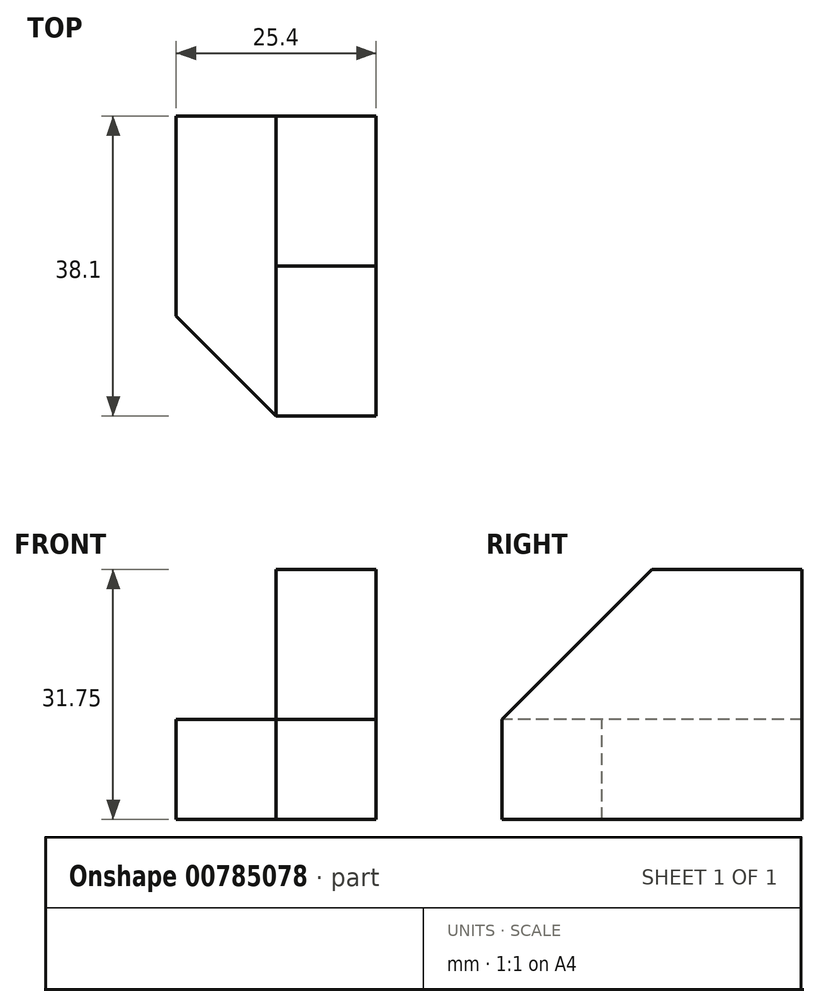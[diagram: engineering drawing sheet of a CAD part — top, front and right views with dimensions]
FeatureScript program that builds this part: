
annotation { "Feature Type Name" : "Feature", "Feature Type Description" : "" }
export const myFeature = defineFeature(function(context is Context, id is Id, definition is map)
    precondition{}
    {
        {
            var Q0;
            Q0=qCreatedBy(makeId("Front.planeOp"),FACE);
            var sketch = newSketch(context, id + "F0", { "sketchPlane" : qUnion([Q0])});
            skLineSegment(sketch, "E0", {"start": v(0, 0) * mm, "end": v(25.4, 0) * mm});
            skLineSegment(sketch, "E1", {"start": v(25.4, 0) * mm, "end": v(25.4, 31.75) * mm});
            skLineSegment(sketch, "E2", {"start": v(25.4, 31.75) * mm, "end": v(0, 31.75) * mm});
            skLineSegment(sketch, "E3", {"start": v(0, 31.75) * mm, "end": v(0, 0) * mm});
            skSolve(sketch);
        }
        {
            var Q0;
            Q0=makeQuery(id+"F0.imprint","IMPRINT",FACE,{"disambiguationData":[TD([[makeQuery(id+"F0.imprint","IMPRINT",EDGE,{"derivedFrom":sQuery(id+"F0.wireOp",EDGE,"E0")}),1.0]])]});
            extrude(context, id + "F1", {"entities" : qUnion([Q0]), "depth" : 38.1 * mm, "offsetDistance" : 25.4 * mm});
        }
        {
            var Q0;
            Q0=makeQuery(id+"F1.opExtrude","CAP_FACE",FACE,{"disambiguationData":[OSD([sQuery(id+"F0.wireOp",EDGE,"E0"),sQuery(id+"F0.wireOp",EDGE,"E1"),sQuery(id+"F0.wireOp",EDGE,"E2"),sQuery(id+"F0.wireOp",EDGE,"E3")])],"isStart":false});
            var sketch = newSketch(context, id + "F2", { "sketchPlane" : qUnion([Q0])});
            skLineSegment(sketch, "E4", {"start": v(25.4, 31.75) * mm, "end": v(12.7, 31.75) * mm});
            skLineSegment(sketch, "E5", {"start": v(12.7, 31.75) * mm, "end": v(12.7, 12.7) * mm});
            skLineSegment(sketch, "E6", {"start": v(12.7, 12.7) * mm, "end": v(0, 12.7) * mm});
            skSolve(sketch);
        }
        {
            var Q0;
            {var subQ0=sQuery(id+"F2.wireOp",EDGE,"E5");Q0=makeQuery(id+"F2.imprint","IMPRINT",FACE,{"disambiguationData":[TD([[makeQuery(id+"F2.imprint","IMPRINT",EDGE,{"derivedFrom":subQ0}),-1.0]])]});}
            extrude(context, id + "F3", {"entities" : qUnion([Q0]), "operationType" : NewBodyOperationType.REMOVE, "oppositeDirection" : true, "depth" : 38.1 * mm, "offsetDistance" : 25.4 * mm});
        }
        {
            var Q0;
            Q0=makeQuery(id+"F3.boolean.opBoolean","COPY",FACE,{"derivedFrom":makeQuery(id+"F3.opExtrude","SWEPT_FACE",FACE,{"disambiguationData":[OSD([sQuery(id+"F2.wireOp",EDGE,"E5")])]})});
            var sketch = newSketch(context, id + "F4", { "sketchPlane" : qUnion([Q0])});
            skLineSegment(sketch, "E7", {"start": v(38.1, 31.75) * mm, "end": v(19.05, 31.75) * mm});
            skLineSegment(sketch, "E8", {"start": v(19.05, 31.75) * mm, "end": v(38.1, 12.7) * mm});
            skSolve(sketch);
        }
        {
            var Q0;
            Q0=makeQuery(id+"F4.imprint","IMPRINT",FACE,{"disambiguationData":[TD([[makeQuery(id+"F4.imprint","IMPRINT",EDGE,{"derivedFrom":sQuery(id+"F4.wireOp",EDGE,"E7")}),-1.0]])]});
            extrude(context, id + "F5", {"entities" : qUnion([Q0]), "operationType" : NewBodyOperationType.REMOVE, "oppositeDirection" : true, "depth" : 25.4 * mm, "offsetDistance" : 25.4 * mm});
        }
        {
            var Q0;
            Q0=makeQuery(id+"F3.boolean.opBoolean","COPY",FACE,{"derivedFrom":makeQuery(id+"F3.opExtrude","SWEPT_FACE",FACE,{"disambiguationData":[OSD([sQuery(id+"F2.wireOp",EDGE,"E6")])]})});
            var sketch = newSketch(context, id + "F6", { "sketchPlane" : qUnion([Q0])});
            skLineSegment(sketch, "E9", {"start": v(0, -38.1) * mm, "end": v(0, -25.4) * mm});
            skLineSegment(sketch, "E10", {"start": v(0, -25.4) * mm, "end": v(12.7, -38.1) * mm});
            skSolve(sketch);
        }
        {
            var Q0;
            Q0=makeQuery(id+"F6.imprint","IMPRINT",FACE,{"disambiguationData":[TD([[makeQuery(id+"F6.imprint","IMPRINT",EDGE,{"derivedFrom":sQuery(id+"F6.wireOp",EDGE,"E9")}),1.0]])]});
            extrude(context, id + "F7", {"entities" : qUnion([Q0]), "operationType" : NewBodyOperationType.REMOVE, "oppositeDirection" : true, "depth" : 25.4 * mm, "offsetDistance" : 25.4 * mm});
        }
    });
